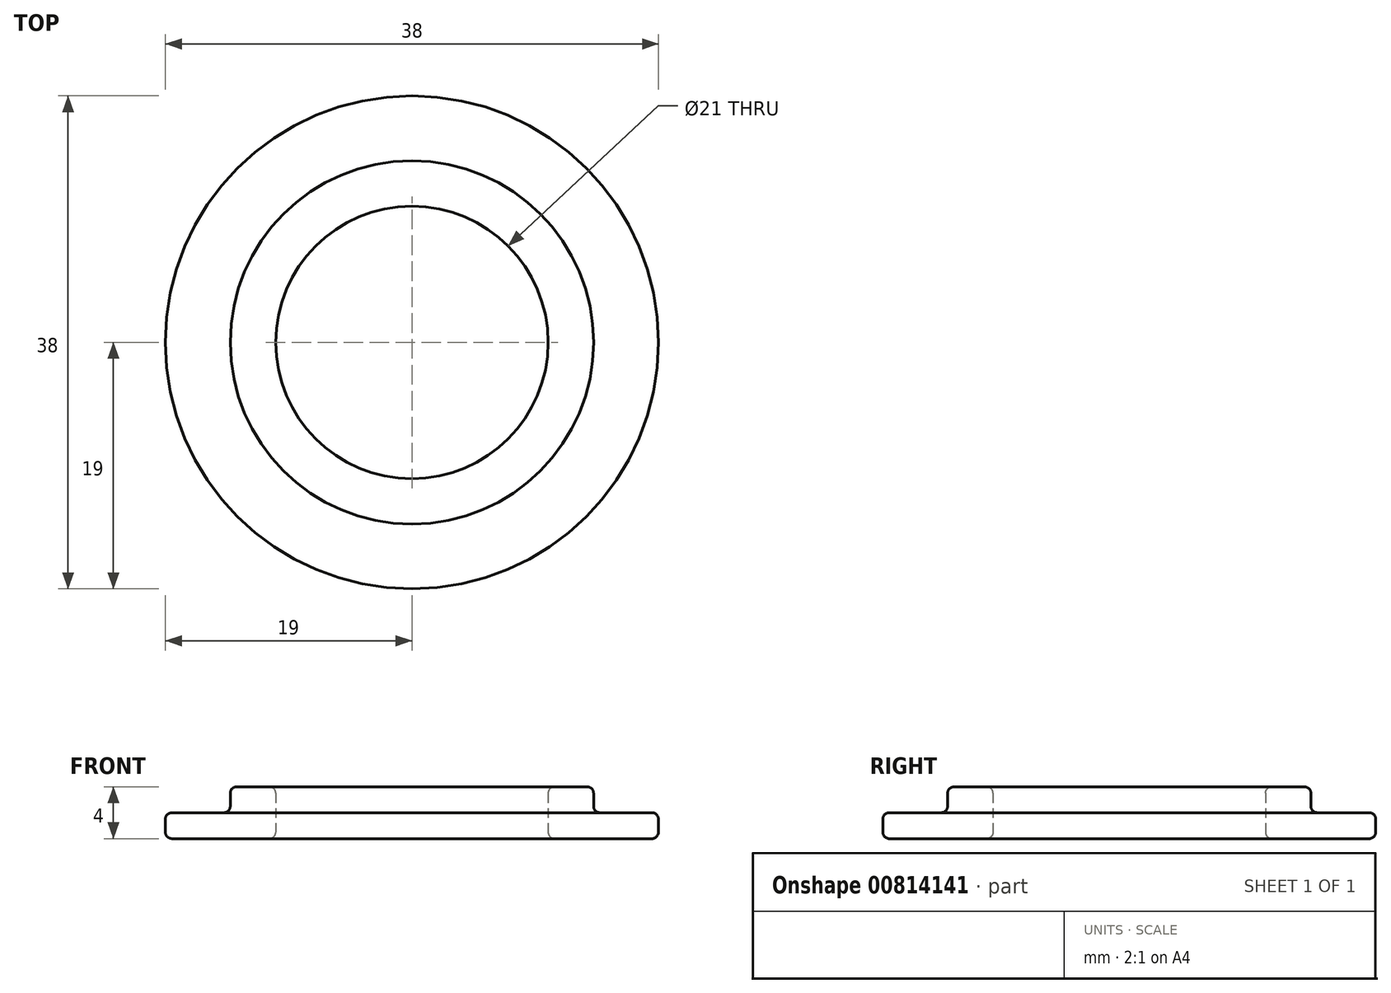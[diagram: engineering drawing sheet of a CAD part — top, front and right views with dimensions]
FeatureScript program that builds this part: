
annotation { "Feature Type Name" : "Feature", "Feature Type Description" : "" }
export const myFeature = defineFeature(function(context is Context, id is Id, definition is map)
    precondition{}
    {
        {
            var Q0;
            Q0=qCreatedBy(makeId("Top.planeOp"),FACE);
            var sketch = newSketch(context, id + "F0", { "sketchPlane" : qUnion([Q0])});
            skCircle(sketch, "E0", {"center": v(0, 0) * mm, "radius": 14 * mm});
            skCircle(sketch, "E1", {"center": v(0, 0) * mm, "radius": 10.5 * mm});
            skSolve(sketch);
        }
        {
            var Q0;
            Q0 = qSketchRegion(id + "F0", true);
            extrude(context, id + "F1", {"entities" : qUnion([Q0]), "depth" : 2 * mm, "offsetDistance" : 25 * mm});
        }
        {
            var Q0;
            Q0=makeQuery(id+"F1.opExtrude","CAP_FACE",FACE,{"disambiguationData":[OSD([sQuery(id+"F0.wireOp",EDGE,"E0"),sQuery(id+"F0.wireOp",EDGE,"E1")])],"isStart":true});
            var sketch = newSketch(context, id + "F2", { "sketchPlane" : qUnion([Q0])});
            skCircle(sketch, "E2", {"center": v(0, 0) * mm, "radius": 10.5 * mm});
            skCircle(sketch, "E3", {"center": v(0, 0) * mm, "radius": 19 * mm});
            skSolve(sketch);
        }
        {
            var Q0;
            Q0 = qSketchRegion(id + "F2", true);
            extrude(context, id + "F3", {"entities" : qUnion([Q0]), "operationType" : NewBodyOperationType.ADD, "depth" : 2 * mm, "offsetDistance" : 25 * mm});
        }
        {
            var Q0;
            Q0=makeQuery(id+"F1.opExtrude","CAP_EDGE",EDGE,{"disambiguationData":[OSD([sQuery(id+"F0.wireOp",EDGE,"E1")])],"isStart":false});
            var Q1;
            Q1=makeQuery(id+"F1.opExtrude","CAP_EDGE",EDGE,{"disambiguationData":[OSD([sQuery(id+"F0.wireOp",EDGE,"E0")])],"isStart":false});
            var Q2;
            Q2=makeQuery(id+"F3.opExtrude","CAP_FACE",FACE,{"disambiguationData":[OSD([sQuery(id+"F2.wireOp",EDGE,"E2"),sQuery(id+"F2.wireOp",EDGE,"E3")])],"isStart":true});
            var Q3;
            Q3=makeQuery(id+"F3.opExtrude","CAP_FACE",FACE,{"disambiguationData":[OSD([sQuery(id+"F2.wireOp",EDGE,"E2"),sQuery(id+"F2.wireOp",EDGE,"E3")])],"isStart":false});
            fillet(context, id + "F4", {"entities" : qUnion([Q0, Q1, Q2, Q3]), "radius" : .5 * mm, "tangentPropagation" : true, "allowEdgeOverflow" : false});
        }
    });
